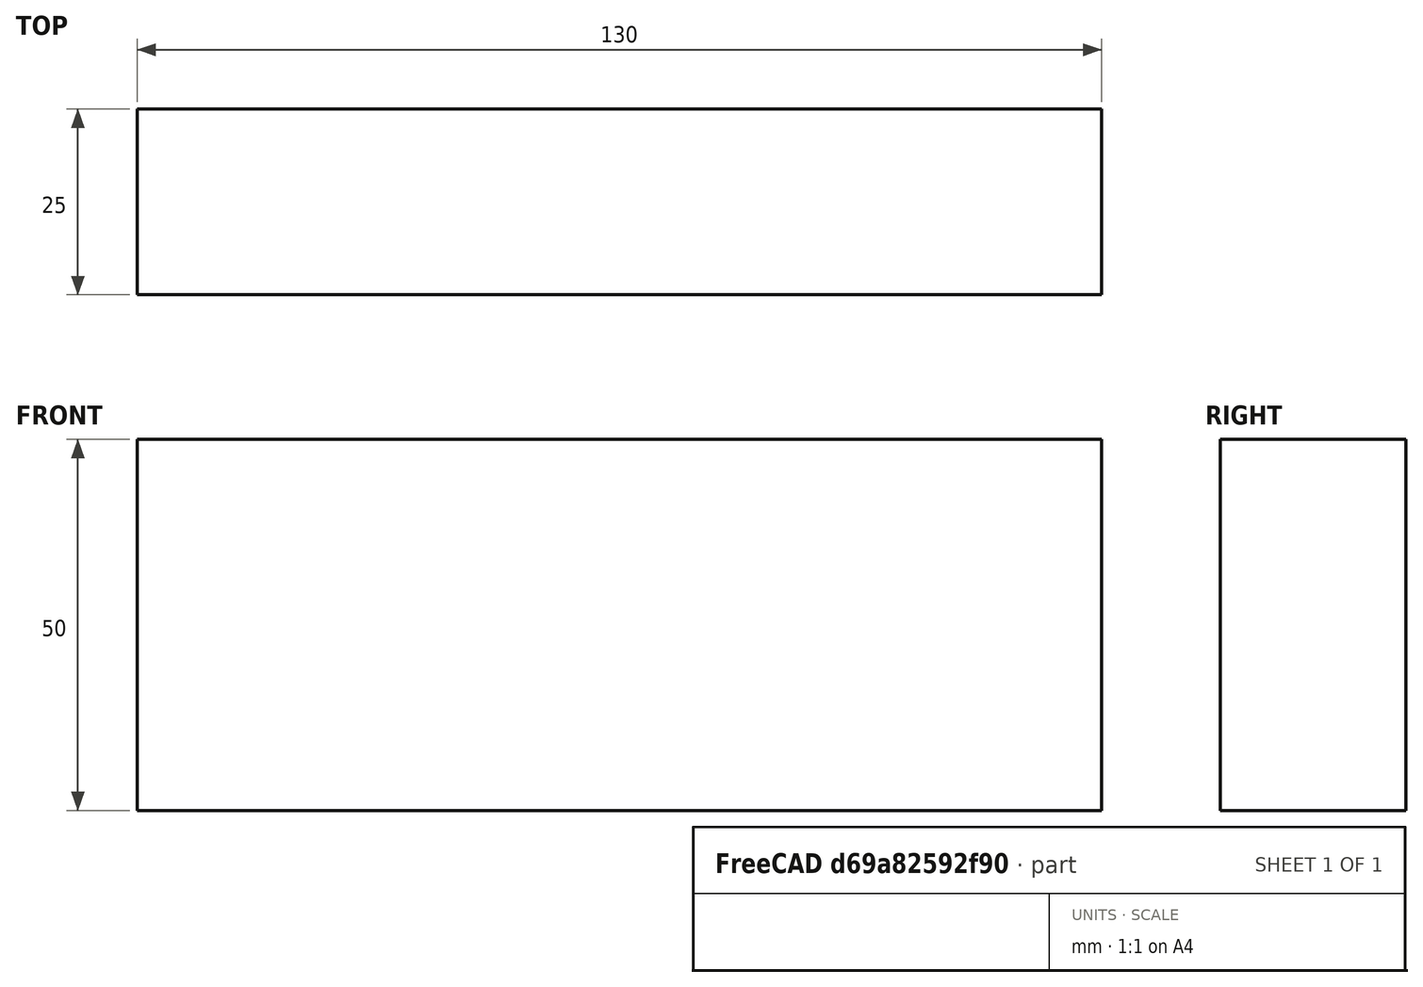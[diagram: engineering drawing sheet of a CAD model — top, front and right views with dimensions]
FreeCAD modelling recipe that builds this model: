
FCSTD DOCUMENT  (FreeCAD 0.15R4671 (Git))
Label: Flat Bar 130x25 EN10058 S235JR
License: All rights reserved
LicenseURL: http://en.wikipedia.org/wiki/All_rights_reserved
objects: Sketcher::SketchObject×1, Part::Extrusion×1
note: 2 computed .brp shape members not serialized (recipe doc carries the construction recipe); baked Part::Feature solids carry a one-line shape summary decoded from their .brp

FEATURE [Sketcher::SketchObject] Sketch
  sketch-geometry (4):
    g0: LineSegment StartX=-65 StartY=-12.5 StartZ=0 EndX=65 EndY=-12.5 EndZ=0
    g1: LineSegment StartX=65 StartY=-12.5 StartZ=0 EndX=65 EndY=12.5 EndZ=0
    g2: LineSegment StartX=65 StartY=12.5 StartZ=0 EndX=-65 EndY=12.5 EndZ=0
    g3: LineSegment StartX=-65 StartY=12.5 StartZ=0 EndX=-65 EndY=-12.5 EndZ=0
  constraints (12):
    c: Coincident(g0,g1)
    c: Coincident(g1,g2)
    c: Coincident(g2,g3)
    c: Coincident(g3,g0)
    c: Horizontal(g0)
    c: Horizontal(g2)
    c: Vertical(g1)
    c: Vertical(g3)
    c: Symmetric(g1,g2,g-2)
    c: Symmetric(g0,g1,g-1)
    c: DistanceY(g1) = 25
    c: DistanceX(g0) = 130
FEATURE [Part::Extrusion] Extrude  label="Flat Bar 130x25 EN10058 S235JR"
  Base = -> Sketch
  Dir = (0,0,50)
  Solid = true
